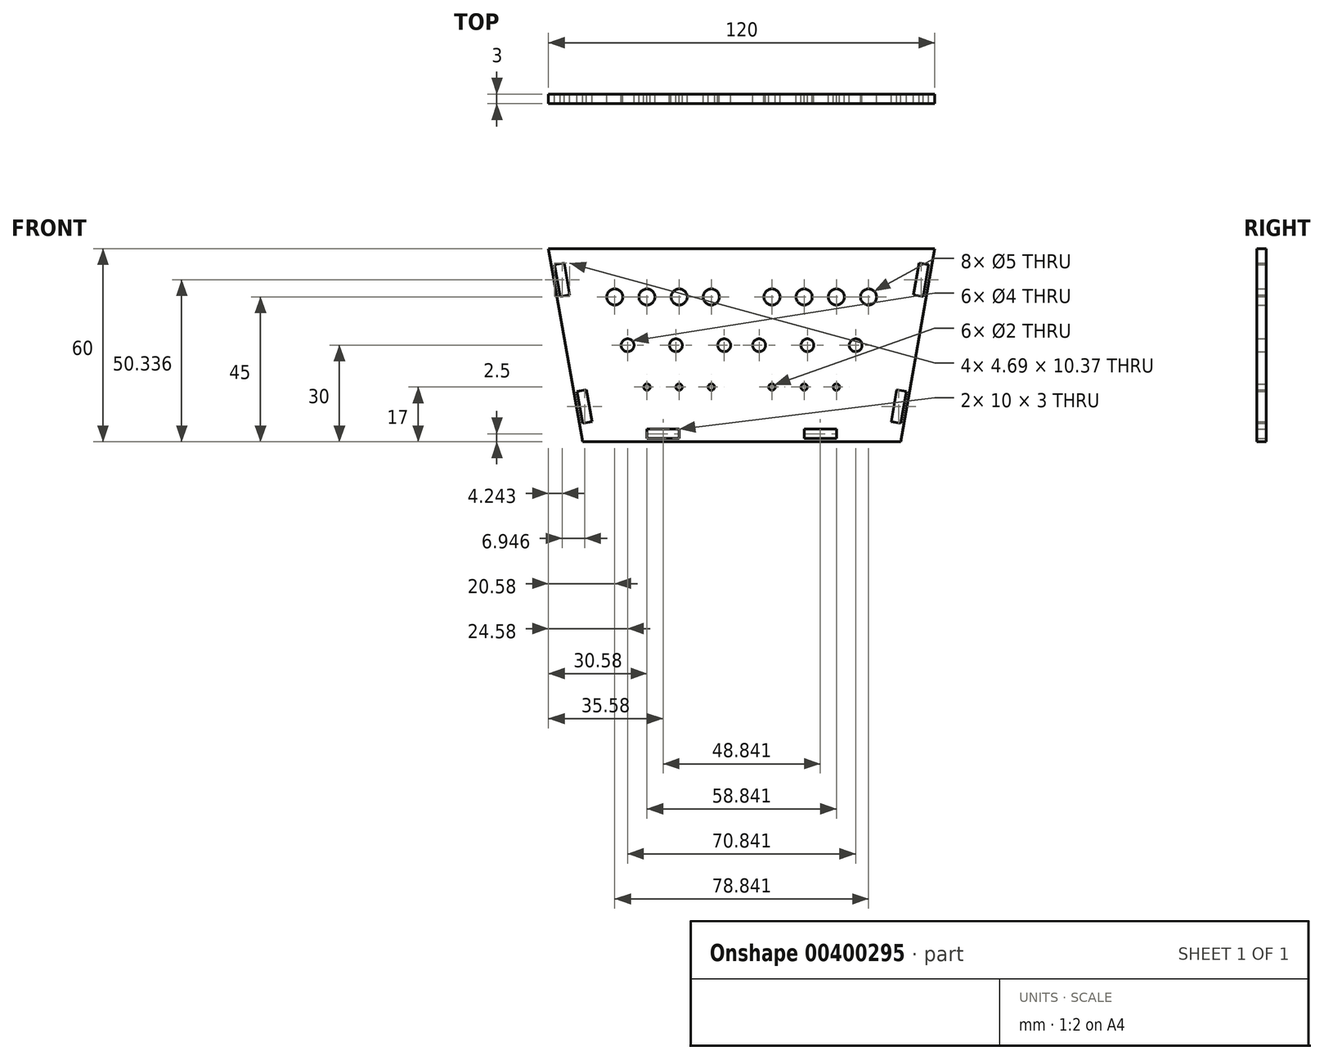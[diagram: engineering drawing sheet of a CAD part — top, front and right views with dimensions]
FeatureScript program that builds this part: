
annotation { "Feature Type Name" : "Feature", "Feature Type Description" : "" }
export const myFeature = defineFeature(function(context is Context, id is Id, definition is map)
    precondition{}
    {
        {
            var Q0;
            Q0=qCreatedBy(makeId("Front.planeOp"),FACE);
            var sketch = newSketch(context, id + "F0", { "sketchPlane" : qUnion([Q0])});
            skLineSegment(sketch, "E0", {"start": v(-49.42, 0) * mm, "end": v(49.42, 0) * mm});
            skLineSegment(sketch, "E1", {"start": v(49.42, 0) * mm, "end": v(60, 60) * mm});
            skLineSegment(sketch, "E2", {"start": v(60, 60) * mm, "end": v(-60, 60) * mm});
            skLineSegment(sketch, "E3", {"start": v(-60, 60) * mm, "end": v(-49.42, 0) * mm});
            skLineSegment(sketch, "E4", {"start": v(0, 0) * mm, "end": v(0, 32) * mm, "construction": true});
            skLineSegment(sketch, "E5", {"start": v(-58.1, 55) * mm, "end": v(-56.37, 45.15) * mm});
            skLineSegment(sketch, "E6", {"start": v(-56.37, 45.15) * mm, "end": v(-53.41, 45.67) * mm});
            skLineSegment(sketch, "E7", {"start": v(-53.41, 45.67) * mm, "end": v(-55.15, 55.52) * mm});
            skLineSegment(sketch, "E8", {"start": v(-55.15, 55.52) * mm, "end": v(-58.1, 55) * mm});
            skLineSegment(sketch, "E9", {"start": v(-51.16, 15.6) * mm, "end": v(-49.42, 5.76) * mm});
            skLineSegment(sketch, "E10", {"start": v(-49.42, 5.76) * mm, "end": v(-46.47, 6.28) * mm});
            skLineSegment(sketch, "E11", {"start": v(-46.47, 6.28) * mm, "end": v(-48.2, 16.13) * mm});
            skLineSegment(sketch, "E12", {"start": v(-48.2, 16.13) * mm, "end": v(-51.16, 15.6) * mm});
            skLineSegment(sketch, "E13.MirrorCS", {"start": v(53.41, 45.67) * mm, "end": v(55.15, 55.52) * mm});
            skLineSegment(sketch, "E14.MirrorCS", {"start": v(56.37, 45.15) * mm, "end": v(53.41, 45.67) * mm});
            skLineSegment(sketch, "E15.MirrorCS", {"start": v(55.15, 55.52) * mm, "end": v(58.1, 55) * mm});
            skLineSegment(sketch, "E16.MirrorCS", {"start": v(58.1, 55) * mm, "end": v(56.37, 45.15) * mm});
            skLineSegment(sketch, "E17.MirrorCS", {"start": v(49.42, 5.76) * mm, "end": v(46.47, 6.28) * mm});
            skLineSegment(sketch, "E18.MirrorCS", {"start": v(46.47, 6.28) * mm, "end": v(48.2, 16.13) * mm});
            skLineSegment(sketch, "E19.MirrorCS", {"start": v(48.2, 16.13) * mm, "end": v(51.16, 15.6) * mm});
            skLineSegment(sketch, "E20.MirrorCS", {"start": v(51.16, 15.6) * mm, "end": v(49.42, 5.76) * mm});
            skLineSegment(sketch, "E21.bottom", {"start": v(-29.42, 1) * mm, "end": v(-19.42, 1) * mm});
            skLineSegment(sketch, "E21.top", {"start": v(-29.42, 4) * mm, "end": v(-19.42, 4) * mm});
            skLineSegment(sketch, "E21.left", {"start": v(-29.42, 1) * mm, "end": v(-29.42, 4) * mm});
            skLineSegment(sketch, "E21.right", {"start": v(-19.42, 1) * mm, "end": v(-19.42, 4) * mm});
            skLineSegment(sketch, "E22.MirrorCS", {"start": v(29.42, 1) * mm, "end": v(19.42, 1) * mm});
            skLineSegment(sketch, "E23.MirrorCS", {"start": v(19.42, 1) * mm, "end": v(19.42, 4) * mm});
            skLineSegment(sketch, "E24.MirrorCS", {"start": v(29.42, 1) * mm, "end": v(29.42, 4) * mm});
            skLineSegment(sketch, "E25.MirrorCS", {"start": v(29.42, 4) * mm, "end": v(19.42, 4) * mm});
            skCircle(sketch, "E26", {"center": v(-39.42, 45) * mm, "radius": 2.5 * mm});
            skLineSegment(sketch, "E27", {"start": v(-39.42, 45) * mm, "end": v(46.65, 45) * mm, "construction": true});
            skLineSegment(sketch, "E28", {"start": v(-43.73, 30) * mm, "end": v(46.05, 30) * mm, "construction": true});
            skLineSegment(sketch, "E29", {"start": v(-33.77, 17) * mm, "end": v(38.47, 17) * mm, "construction": true});
            skCircle(sketch, "E30", {"center": v(-29.42, 45) * mm, "radius": 2.5 * mm});
            skCircle(sketch, "E31", {"center": v(-19.42, 45) * mm, "radius": 2.5 * mm});
            skCircle(sketch, "E32", {"center": v(-9.42, 45) * mm, "radius": 2.5 * mm});
            skCircle(sketch, "E33", {"center": v(-35.42, 30) * mm, "radius": 2 * mm});
            skCircle(sketch, "E34", {"center": v(-20.42, 30) * mm, "radius": 2 * mm});
            skCircle(sketch, "E35", {"center": v(-5.42, 30) * mm, "radius": 2 * mm});
            skCircle(sketch, "E36", {"center": v(-29.42, 17) * mm, "radius": 1 * mm});
            skCircle(sketch, "E37", {"center": v(-19.42, 17) * mm, "radius": 1 * mm});
            skCircle(sketch, "E38", {"center": v(-9.42, 17) * mm, "radius": 1 * mm});
            skCircle(sketch, "E39.MirrorC", {"center": v(9.42, 17) * mm, "radius": 1 * mm});
            skCircle(sketch, "E40.MirrorC", {"center": v(19.42, 17) * mm, "radius": 1 * mm});
            skCircle(sketch, "E41.MirrorC", {"center": v(29.42, 17) * mm, "radius": 1 * mm});
            skCircle(sketch, "E42.MirrorC", {"center": v(5.42, 30) * mm, "radius": 2 * mm});
            skCircle(sketch, "E43.MirrorC", {"center": v(20.42, 30) * mm, "radius": 2 * mm});
            skCircle(sketch, "E44.MirrorC", {"center": v(35.42, 30) * mm, "radius": 2 * mm});
            skCircle(sketch, "E45.MirrorC", {"center": v(9.42, 45) * mm, "radius": 2.5 * mm});
            skCircle(sketch, "E46.MirrorC", {"center": v(29.42, 45) * mm, "radius": 2.5 * mm});
            skCircle(sketch, "E47.MirrorC", {"center": v(39.42, 45) * mm, "radius": 2.5 * mm});
            skCircle(sketch, "E48.MirrorC", {"center": v(19.42, 45) * mm, "radius": 2.5 * mm});
            skLineSegment(sketch, "E49", {"start": v(-29.42, 1) * mm, "end": v(-49.6, 1) * mm, "construction": true});
            skLineSegment(sketch, "E50", {"start": v(-49.6, 1) * mm, "end": v(49.6, 1) * mm, "construction": true});
            skLineSegment(sketch, "E51", {"start": v(46.47, 6.28) * mm, "end": v(45.54, 1) * mm, "construction": true});
            skLineSegment(sketch, "E52", {"start": v(-49.42, 5.76) * mm, "end": v(-48.58, 1) * mm, "construction": true});
            skLineSegment(sketch, "E53", {"start": v(-46.47, 6.28) * mm, "end": v(-45.54, 1) * mm, "construction": true});
            skLineSegment(sketch, "E54", {"start": v(49.42, 5.76) * mm, "end": v(48.58, 1) * mm, "construction": true});
            skLineSegment(sketch, "E55", {"start": v(29.42, 4) * mm, "end": v(46.06, 4) * mm, "construction": true});
            skLineSegment(sketch, "E56", {"start": v(46.06, 4) * mm, "end": v(-46.06, 4) * mm, "construction": true});
            skSolve(sketch);
        }
        {
            var Q0;
            Q0=makeQuery(id+"F0.imprint","IMPRINT",FACE,{"disambiguationData":[TD([[makeQuery(id+"F0.imprint","IMPRINT",EDGE,{"derivedFrom":sQuery(id+"F0.wireOp",EDGE,"E0")}),1.0]])]});
            extrude(context, id + "F1", {"entities" : qUnion([Q0]), "depth" : 3 * mm});
        }
    });
